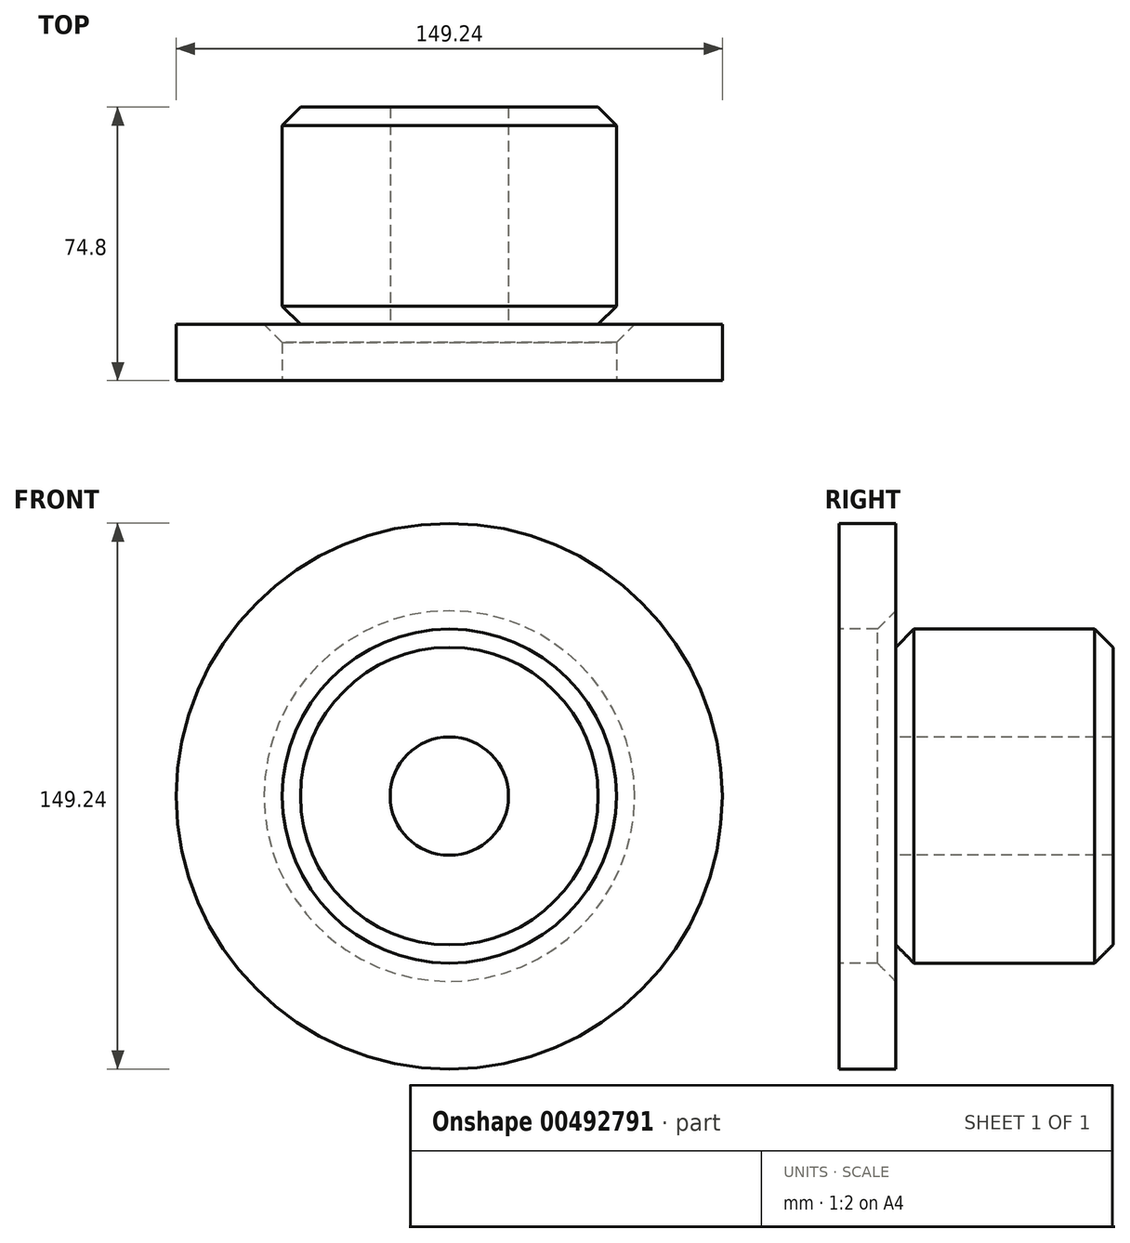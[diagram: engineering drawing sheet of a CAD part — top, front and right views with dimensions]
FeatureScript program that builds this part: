
annotation { "Feature Type Name" : "Feature", "Feature Type Description" : "" }
export const myFeature = defineFeature(function(context is Context, id is Id, definition is map)
    precondition{}
    {
        {
            var Q0;
            Q0=qCreatedBy(makeId("Right.planeOp"),FACE);
            var sketch = newSketch(context, id + "F0", { "sketchPlane" : qUnion([Q0])});
            skLineSegment(sketch, "E0", {"start": v(0, 0) * mm, "end": v(74.8, 0) * mm, "construction": true});
            skLineSegment(sketch, "E1.bottom", {"start": v(0, 16.16) * mm, "end": v(15.41, 16.16) * mm});
            skLineSegment(sketch, "E1.top", {"start": v(0, 74.62) * mm, "end": v(15.41, 74.62) * mm});
            skLineSegment(sketch, "E1.left", {"start": v(0, 16.16) * mm, "end": v(0, 74.62) * mm});
            skLineSegment(sketch, "E1.right", {"start": v(15.41, 16.16) * mm, "end": v(15.41, 74.62) * mm});
            skLineSegment(sketch, "E2.bottom", {"start": v(0, 16.16) * mm, "end": v(74.8, 16.16) * mm});
            skLineSegment(sketch, "E2.top", {"start": v(0, 45.67) * mm, "end": v(74.8, 45.67) * mm});
            skLineSegment(sketch, "E2.left", {"start": v(0, 16.16) * mm, "end": v(0, 45.67) * mm});
            skLineSegment(sketch, "E2.right", {"start": v(74.8, 16.16) * mm, "end": v(74.8, 45.67) * mm});
            skLineSegment(sketch, "E3.MirrorCS", {"start": v(0, -16.16) * mm, "end": v(15.41, -16.16) * mm});
            skLineSegment(sketch, "E4.MirrorCS", {"start": v(0, -45.67) * mm, "end": v(74.8, -45.67) * mm});
            skLineSegment(sketch, "E5.MirrorCS", {"start": v(0, -74.62) * mm, "end": v(15.41, -74.62) * mm});
            skLineSegment(sketch, "E6.MirrorCS", {"start": v(0, -16.16) * mm, "end": v(0, -74.62) * mm});
            skLineSegment(sketch, "E7.MirrorCS", {"start": v(15.41, -16.16) * mm, "end": v(15.41, -74.62) * mm});
            skLineSegment(sketch, "E8.MirrorCS", {"start": v(0, -16.16) * mm, "end": v(74.8, -16.16) * mm});
            skLineSegment(sketch, "E9.MirrorCS", {"start": v(74.8, -16.16) * mm, "end": v(74.8, -45.67) * mm});
            skLineSegment(sketch, "E10.MirrorCS", {"start": v(0, -16.16) * mm, "end": v(0, -45.67) * mm});
            skSolve(sketch);
        }
        {
            var Q0;
            {var subQ5=sQuery(id+"F0.wireOp",EDGE,"E2.left");Q0=makeQuery(id+"F0.imprint","IMPRINT",FACE,{"disambiguationData":[TD([[makeQuery(id+"F0.imprint","IMPRINT",EDGE,{"derivedFrom":subQ5}),-1.0]])]});}
            var Q1;
            {var subQ5=sQuery(id+"F0.wireOp",EDGE,"E2.right");Q1=makeQuery(id+"F0.imprint","IMPRINT",FACE,{"disambiguationData":[TD([[makeQuery(id+"F0.imprint","IMPRINT",EDGE,{"derivedFrom":subQ5}),1.0]])]});}
            var Q2;
            {var subQ0=sQuery(id+"F0.wireOp",EDGE,"E1.top");Q2=makeQuery(id+"F0.imprint","IMPRINT",FACE,{"disambiguationData":[TD([[makeQuery(id+"F0.imprint","IMPRINT",EDGE,{"derivedFrom":subQ0}),-1.0]])]});}
            var Q3;
            Q3=sQuery(id+"F0.wireOp",EDGE,"E0");
            revolve(context, id + "F1", {"entities" : qUnion([Q0, Q1, Q2]), "axis" : qUnion([Q3]), "revolveType" : RevolveType.FULL});
        }
        {
            var Q0;
            Q0=makeQuery(id+"F1.opRevolve","SWEPT_EDGE",EDGE,{"disambiguationData":[OSD([sQuery(id+"F0.wireOp",EDGE,"E1.right"),sQuery(id+"F0.wireOp",EDGE,"E2.top")])]});
            var Q1;
            Q1=makeQuery(id+"F1.opRevolve","SWEPT_EDGE",EDGE,{"disambiguationData":[OSD([sQuery(id+"F0.wireOp",EDGE,"E2.top"),sQuery(id+"F0.wireOp",EDGE,"E2.right")])]});
            chamfer(context, id + "F2", {"entities" : qUnion([Q0, Q1]), "width" : 5 * mm, "tangentPropagation" : true});
        }
    });
